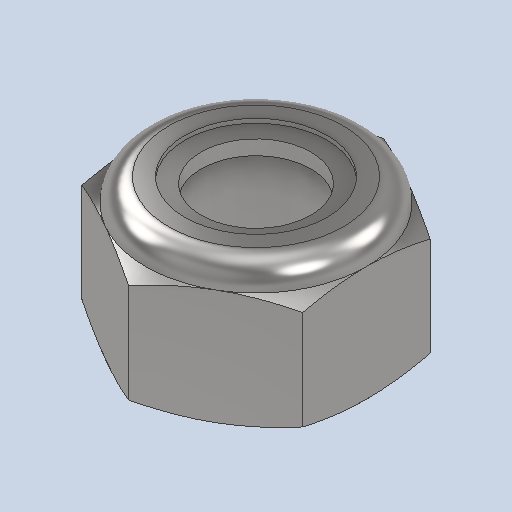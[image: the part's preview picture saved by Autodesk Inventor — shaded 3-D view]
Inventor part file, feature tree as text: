
AUTODESK INVENTOR PART (.ipt)
format: ipt  version: 2023 (Build 270158030, 158C)  size: 215,040 bytes
history: native  units: in
note: dims shown in document units (in); Inventor stores cm internally (conversion verified against a paired STEP export)
features: other x1, revolve x1
ambient origin geometry x8: Origin, YZ Plane, XZ Plane, XY Plane, X Axis, Y Axis, Z Axis, Center Point
bodies: Solid1 (feature_tree), Solid2 (feature_tree)
feature tree (2):
  other  "Cut-Revolve4"
  revolve  "Revolve2"  [1 undecoded]
note: 1 required parameter value undecoded (feature->parameter linkage not recoverable at this tier; creation-order binding heuristic only, values carry confidence <= 0.55)
